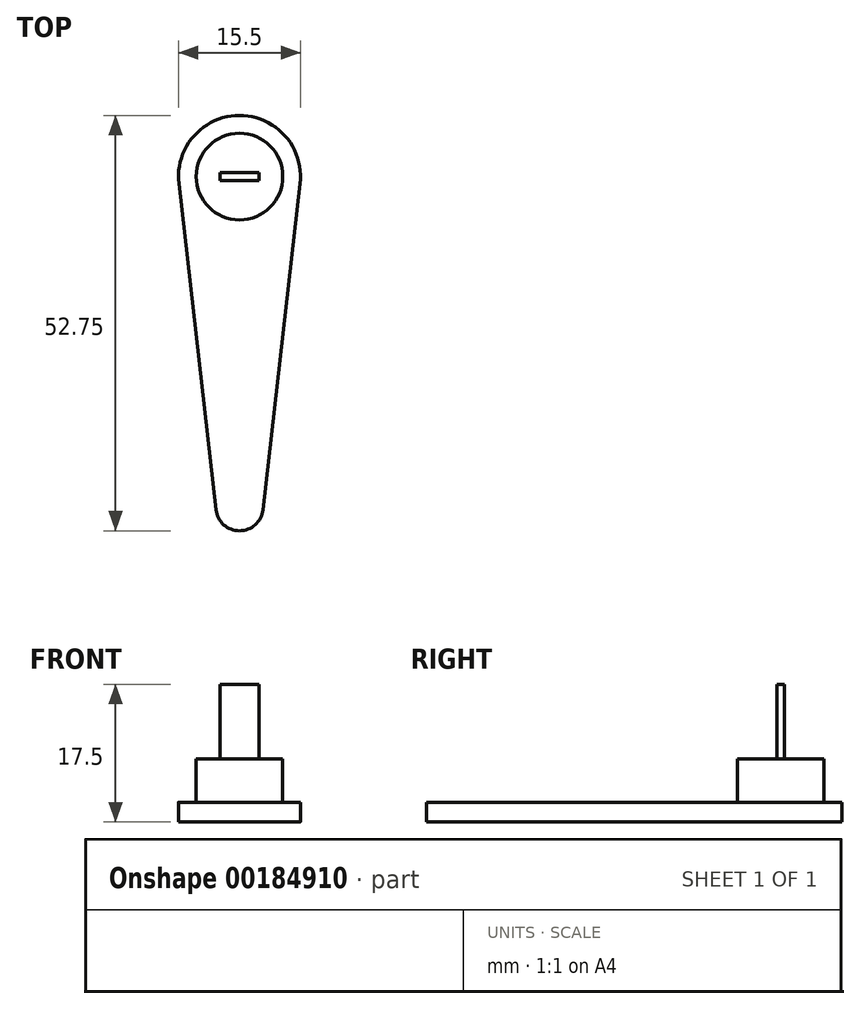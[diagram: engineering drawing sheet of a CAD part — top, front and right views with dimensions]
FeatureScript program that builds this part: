
annotation { "Feature Type Name" : "Feature", "Feature Type Description" : "" }
export const myFeature = defineFeature(function(context is Context, id is Id, definition is map)
    precondition{}
    {
        {
            var Q0;
            Q0=qCreatedBy(makeId("Top.planeOp"),FACE);
            var sketch = newSketch(context, id + "F0", { "sketchPlane" : qUnion([Q0])});
            skLineSegment(sketch, "E0.bottom", {"start": v(-2.5, -0.5) * mm, "end": v(2.5, -0.5) * mm});
            skLineSegment(sketch, "E0.top", {"start": v(-2.5, 0.5) * mm, "end": v(2.5, 0.5) * mm});
            skLineSegment(sketch, "E0.left", {"start": v(-2.5, 0.5) * mm, "end": v(-2.5, -0.5) * mm});
            skLineSegment(sketch, "E0.right", {"start": v(2.5, 0.5) * mm, "end": v(2.5, -0.5) * mm});
            skCircle(sketch, "E1", {"center": v(0, 0) * mm, "radius": 5.5 * mm});
            skCircle(sketch, "E2", {"center": v(0, 0) * mm, "radius": 7.75 * mm});
            skCircle(sketch, "E3", {"center": v(0, -42) * mm, "radius": 3 * mm});
            skLineSegment(sketch, "E4", {"start": v(-7.7, -0.88) * mm, "end": v(-2.98, -42.34) * mm});
            skLineSegment(sketch, "E5", {"start": v(7.7, -0.88) * mm, "end": v(2.98, -42.34) * mm});
            skSolve(sketch);
        }
        {
            var Q0;
            Q0=makeQuery(id+"F0.imprint","IMPRINT",FACE,{"disambiguationData":[TD([[makeQuery(id+"F0.imprint","IMPRINT",EDGE,{"derivedFrom":sQuery(id+"F0.wireOp",EDGE,"E0.bottom")}),1.0]])]});
            extrude(context, id + "F1", {"entities" : qUnion([Q0]), "depth" : 15 * mm});
        }
        {
            var Q0;
            Q0=makeQuery(id+"F0.imprint","IMPRINT",FACE,{"disambiguationData":[TD([[makeQuery(id+"F0.imprint","IMPRINT",EDGE,{"derivedFrom":sQuery(id+"F0.wireOp",EDGE,"E0.bottom")}),-1.0]])]});
            extrude(context, id + "F2", {"entities" : qUnion([Q0]), "operationType" : NewBodyOperationType.ADD, "depth" : 5.5 * mm});
        }
        {
            var Q0;
            {var subQ0=sQuery(id+"F0.wireOp",EDGE,"E4");Q0=makeQuery(id+"F0.imprint","IMPRINT",FACE,{"disambiguationData":[TD([[makeQuery(id+"F0.imprint","IMPRINT",EDGE,{"derivedFrom":subQ0}),1.0]])]});}
            var Q1;
            {var subQ0=sQuery(id+"F0.wireOp",EDGE,"E3");var subQ1=makeQuery(id+"F0.imprint","INTERSECT",VERTEX,{"derivedFrom":[subQ0,sQuery(id+"F0.wireOp",EDGE,"E4")]});Q1=makeQuery(id+"F0.imprint","IMPRINT",FACE,{"disambiguationData":[TD([[makeQuery(id+"F0.imprint","IMPRINT",EDGE,{"disambiguationData":[TD([[subQ1,-1.0]])],"derivedFrom":subQ0}),1.0]])]});}
            var Q2;
            Q2=makeQuery(id+"F0.imprint","IMPRINT",FACE,{"disambiguationData":[TD([[makeQuery(id+"F0.imprint","IMPRINT",EDGE,{"derivedFrom":sQuery(id+"F0.wireOp",EDGE,"E0.bottom")}),1.0]])]});
            var Q3;
            Q3=makeQuery(id+"F0.imprint","IMPRINT",FACE,{"disambiguationData":[TD([[makeQuery(id+"F0.imprint","IMPRINT",EDGE,{"derivedFrom":sQuery(id+"F0.wireOp",EDGE,"E0.bottom")}),-1.0]])]});
            var Q4;
            Q4=makeQuery(id+"F0.imprint","IMPRINT",FACE,{"disambiguationData":[TD([[makeQuery(id+"F0.imprint","IMPRINT",EDGE,{"derivedFrom":sQuery(id+"F0.wireOp",EDGE,"E1")}),-1.0]])]});
            extrude(context, id + "F3", {"entities" : qUnion([Q0, Q1, Q2, Q3, Q4]), "operationType" : NewBodyOperationType.ADD, "oppositeDirection" : true, "depth" : 2.5 * mm});
        }
    });
